# Revit family: 111012001058001
name_source: partatom
category: Modelos genéricos
revit_build: Autodesk Revit 2018 (Build: 20190510_1515(x64)
units: mm (PartAtom-declared; Revit-internal decimal feet)

## family parameters
Compartido = No
Corte con vacíos al cargar = No
Cota de conector redondo = Diámetro de uso
Puede alojar armadura = No
Punto de cálculo de habitación = No
Se basa en plano de trabajo = No
Siempre vertical = No
Tipo de pieza = Normal

## types (1)
- SELLO TINA PVC 25X23MM BLANCO TIRA 3MT
    Aplicacion = Se utiliza como terminación en las tinas de los baños
    Color = Blanco o Café
    Descripción = Se utiliza como terminación en las tinas de los baños
    Dimension = 25 mm  [stored 0.082021 ft]
    Dureza = Shore D 80
    Empresa = CNP SPA.
    Espesor = 1.5 mm  [stored 0.00492126 ft]
    Largo = 3000 mm  [stored 9.84252 ft]
    Material = PVC Rígido Coextruído con PVC Flexible blanco
    Modelo = SELLO TINA PVC 25X23MM
    Nombre SKU = SELLO TINA PVC 25X23MM BLANCO TIRA 3MT
    Num SKUs = 111012001058001
    URL = https://www.empresascnp.cl
    Unidad = Tira 3.00 mts.
    Url Ficha tecnica = https://empresascnp.cl
    Uso = Se utiliza como terminación en las tinas de los baños.
Reemplazando la silicona gracias a sus aletas flexibles de PVC
que permiten generar un sello evitando filtraciones
    Ventajas = Autoextinguible

note: [stored X ft] marks values corroborated as IEEE doubles in the binary element streams (Revit-internal decimal feet)

## geometry (parser evidence)
native form markers: Sweep x2
no freeform markers — native parametric forms only
